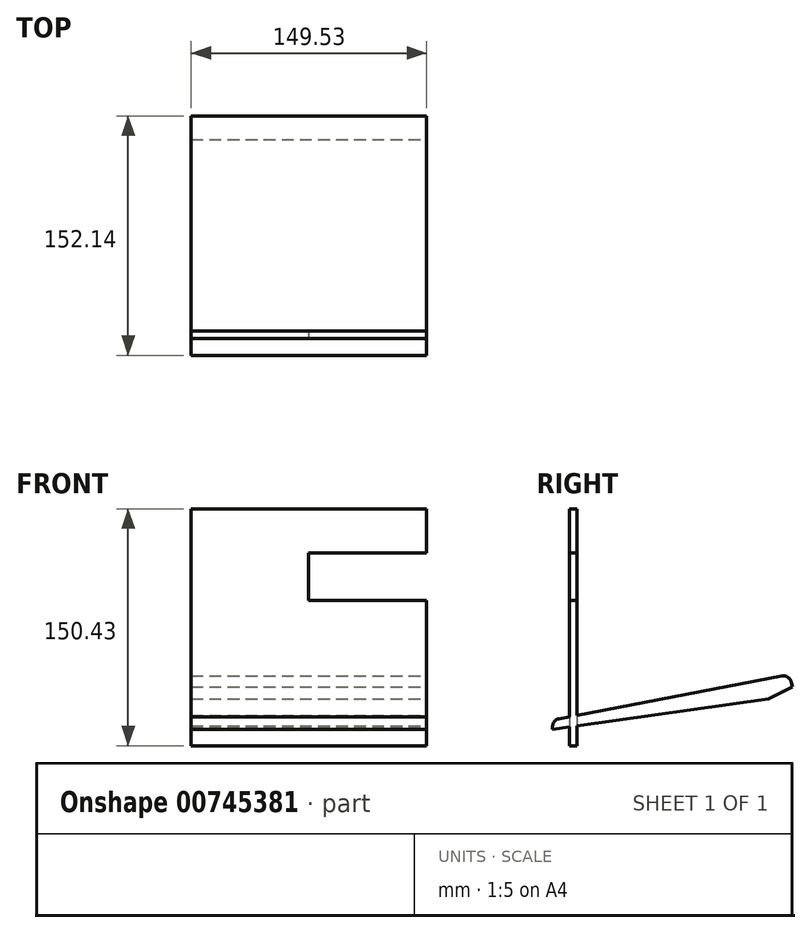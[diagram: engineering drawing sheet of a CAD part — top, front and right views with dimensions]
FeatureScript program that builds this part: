
annotation { "Feature Type Name" : "Feature", "Feature Type Description" : "" }
export const myFeature = defineFeature(function(context is Context, id is Id, definition is map)
    precondition{}
    {
        {
            var Q0;
            Q0=qCreatedBy(makeId("Front.planeOp"),FACE);
            var sketch = newSketch(context, id + "F0", { "sketchPlane" : qUnion([Q0])});
            skLineSegment(sketch, "E0.bottom", {"start": v(-74.33, 74.73) * mm, "end": v(75.2, 74.73) * mm});
            skLineSegment(sketch, "E0.top", {"start": v(-74.33, -75.7) * mm, "end": v(75.2, -75.7) * mm});
            skLineSegment(sketch, "E0.left", {"start": v(-74.33, 74.73) * mm, "end": v(-74.33, -75.7) * mm});
            skLineSegment(sketch, "E0.right", {"start": v(75.2, 74.73) * mm, "end": v(75.2, -75.7) * mm});
            skSolve(sketch);
        }
        {
            var Q0;
            Q0=makeQuery(id+"F0.imprint","IMPRINT",FACE,{"disambiguationData":[TD([[makeQuery(id+"F0.imprint","IMPRINT",EDGE,{"derivedFrom":sQuery(id+"F0.wireOp",EDGE,"E0.bottom")}),-1.0]])]});
            extrude(context, id + "F1", {"entities" : qUnion([Q0]), "depth" : 4.8 * mm, "offsetDistance" : 25 * mm});
        }
        {
            var Q0;
            Q0=makeQuery(id+"F1.opExtrude","CAP_FACE",FACE,{"disambiguationData":[OSD([sQuery(id+"F0.wireOp",EDGE,"E0.bottom"),sQuery(id+"F0.wireOp",EDGE,"E0.top"),sQuery(id+"F0.wireOp",EDGE,"E0.left"),sQuery(id+"F0.wireOp",EDGE,"E0.right")])],"isStart":false});
            var sketch = newSketch(context, id + "F2", { "sketchPlane" : qUnion([Q0])});
            skLineSegment(sketch, "E1.bottom", {"start": v(75.2, 16.47) * mm, "end": v(0, 16.47) * mm});
            skLineSegment(sketch, "E1.top", {"start": v(75.2, 46.82) * mm, "end": v(0, 46.82) * mm});
            skLineSegment(sketch, "E1.left", {"start": v(75.2, 16.47) * mm, "end": v(75.2, 46.82) * mm});
            skLineSegment(sketch, "E1.right", {"start": v(0, 16.47) * mm, "end": v(0, 46.82) * mm});
            skSolve(sketch);
        }
        {
            var Q0;
            Q0 = qSketchRegion(id + "F2", true);
            extrude(context, id + "F3", {"entities" : qUnion([Q0]), "operationType" : NewBodyOperationType.REMOVE, "oppositeDirection" : true, "depth" : 33 * mm, "offsetDistance" : 25 * mm});
        }
        {
            var Q0;
            {var subQ0=sQuery(id+"F0.wireOp",EDGE,"E0.right");var subQ2=sQuery(id+"F0.wireOp",EDGE,"E0.top");Q0=makeQuery(id+"F3.boolean.opBoolean","SPLIT",FACE,{"disambiguationData":[TD([makeQuery(id+"F1.opExtrude","SWEPT_FACE",FACE,{"disambiguationData":[OSD([subQ2])]})])],"derivedFrom":makeQuery(id+"F1.opExtrude","SWEPT_FACE",FACE,{"disambiguationData":[OSD([subQ0])]})});}
            var sketch = newSketch(context, id + "F4", { "sketchPlane" : qUnion([Q0])});
            skLineSegment(sketch, "E2", {"start": v(-15.48, -65.2) * mm, "end": v(-15.48, -63.46) * mm});
            skLineSegment(sketch, "E3", {"start": v(-11.41, -58.55) * mm, "end": v(130.27, -31.53) * mm});
            skLineSegment(sketch, "E4", {"start": v(136.12, -35.5) * mm, "end": v(136.66, -38.34) * mm});
            skLineSegment(sketch, "E5", {"start": v(-15.48, -65.2) * mm, "end": v(121.53, -45.98) * mm});
            skLineSegment(sketch, "E6", {"start": v(121.53, -45.98) * mm, "end": v(136.66, -38.34) * mm});
            skPoint(sketch, "E7.visualSharp", {"position": v(135.18, -30.6) * mm});
            skArc(sketch, "E7.filletArc", {"start": v(136.12, -35.5) * mm, "mid": v(134.02, -32.3) * mm, "end": v(130.27, -31.53) * mm});
            skPoint(sketch, "E8.visualSharp", {"position": v(-15.48, -59.32) * mm});
            skArc(sketch, "E8.filletArc", {"start": v(-11.41, -58.55) * mm, "mid": v(-14.33, -60.27) * mm, "end": v(-15.48, -63.46) * mm});
            skSolve(sketch);
        }
        {
            var Q0;
            Q0=makeQuery(id+"F4.imprint","IMPRINT",FACE,{"disambiguationData":[TD([[makeQuery(id+"F4.imprint","IMPRINT",EDGE,{"derivedFrom":sQuery(id+"F4.wireOp",EDGE,"E4")}),-1.0]])]});
            var Q1;
            {var subQ7=sQuery(id+"F4.wireOp",EDGE,"E2");Q1=makeQuery(id+"F4.imprint","IMPRINT",FACE,{"disambiguationData":[TD([[makeQuery(id+"F4.imprint","IMPRINT",EDGE,{"derivedFrom":subQ7}),-1.0]])]});}
            extrude(context, id + "F5", {"entities" : qUnion([Q0, Q1]), "operationType" : NewBodyOperationType.ADD, "oppositeDirection" : true, "depth" : 149.5 * mm, "offsetDistance" : 25 * mm});
        }
    });
